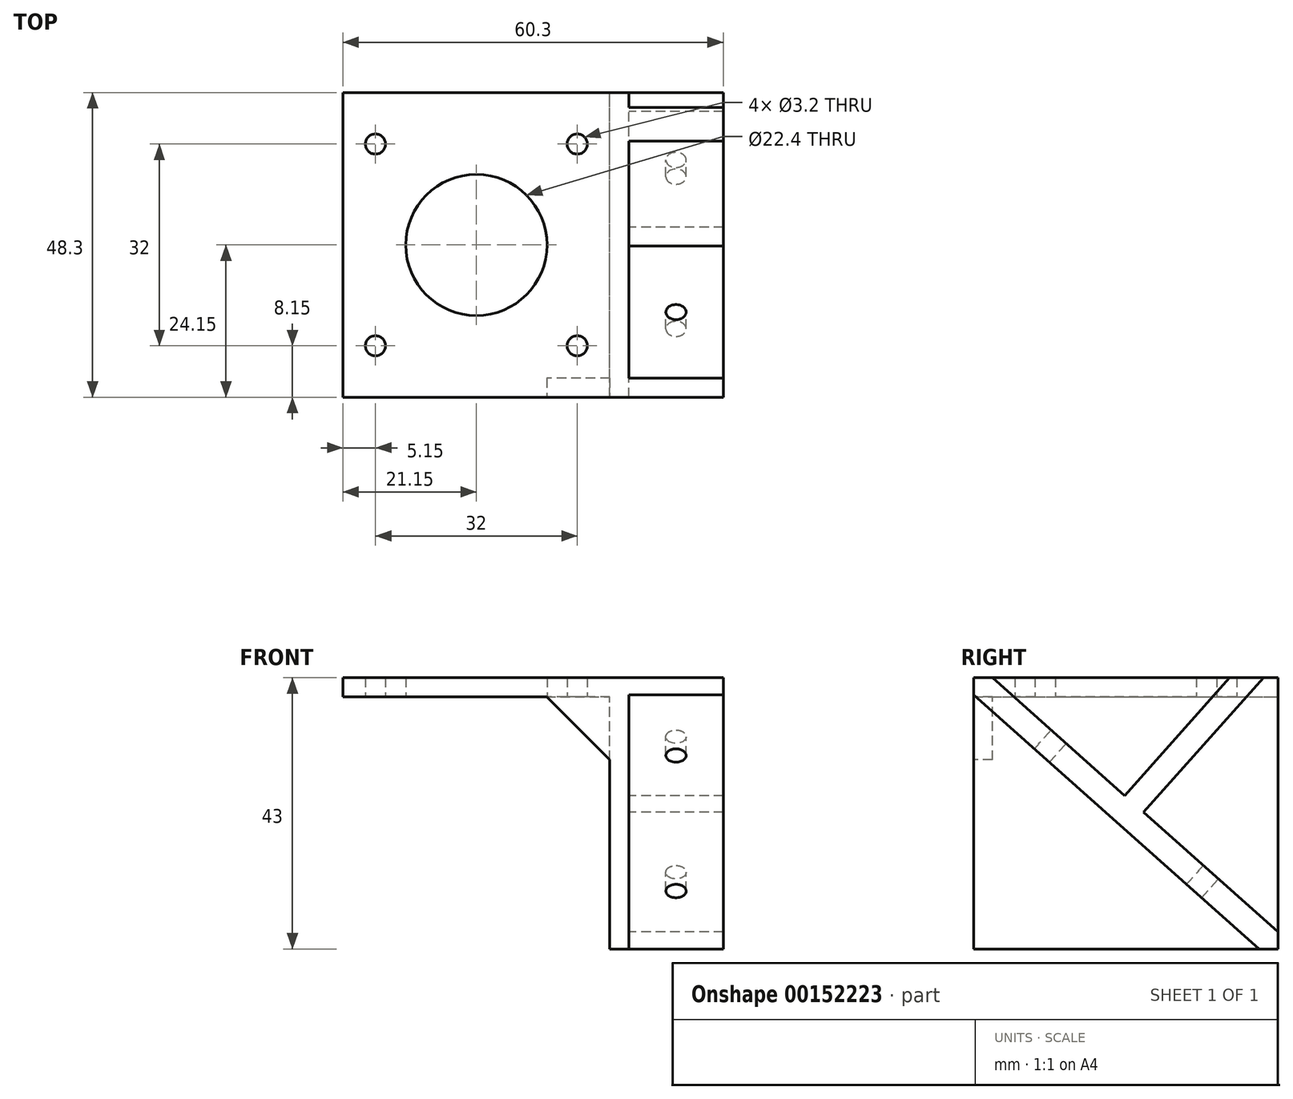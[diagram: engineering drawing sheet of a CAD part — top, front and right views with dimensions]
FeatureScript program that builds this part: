
annotation { "Feature Type Name" : "Feature", "Feature Type Description" : "" }
export const myFeature = defineFeature(function(context is Context, id is Id, definition is map)
    precondition{}
    {
        {
            var Q0;
            Q0=qCreatedBy(makeId("Top.planeOp"),FACE);
            var sketch = newSketch(context, id + "F0", { "sketchPlane" : qUnion([Q0])});
            skCircle(sketch, "E0", {"center": v(0, 0) * mm, "radius": 11.2 * mm});
            skLineSegment(sketch, "E1.bottom", {"start": v(21.15, 21.15) * mm, "end": v(-21.15, 21.15) * mm});
            skLineSegment(sketch, "E1.top", {"start": v(21.15, -21.15) * mm, "end": v(-21.15, -21.15) * mm});
            skLineSegment(sketch, "E1.left", {"start": v(21.15, 21.15) * mm, "end": v(21.15, -21.15) * mm});
            skLineSegment(sketch, "E1.right", {"start": v(-21.15, 21.15) * mm, "end": v(-21.15, -21.15) * mm});
            skLineSegment(sketch, "E2.bottom", {"start": v(16, 16) * mm, "end": v(-16, 16) * mm});
            skLineSegment(sketch, "E2.top", {"start": v(16, -16) * mm, "end": v(-16, -16) * mm});
            skLineSegment(sketch, "E2.left", {"start": v(16, 16) * mm, "end": v(16, -16) * mm});
            skLineSegment(sketch, "E2.right", {"start": v(-16, 16) * mm, "end": v(-16, -16) * mm});
            skCircle(sketch, "E3", {"center": v(-16, 16) * mm, "radius": 1.6 * mm});
            skCircle(sketch, "E4", {"center": v(-16, -16) * mm, "radius": 1.6 * mm});
            skCircle(sketch, "E5", {"center": v(16, -16) * mm, "radius": 1.6 * mm});
            skCircle(sketch, "E6", {"center": v(16, 16) * mm, "radius": 1.6 * mm});
            skLineSegment(sketch, "E7.bottom", {"start": v(-21.15, 21.15) * mm, "end": v(21.15, 21.15) * mm});
            skLineSegment(sketch, "E7.top", {"start": v(-21.15, 24.15) * mm, "end": v(21.15, 24.15) * mm});
            skLineSegment(sketch, "E7.left", {"start": v(-21.15, 21.15) * mm, "end": v(-21.15, 24.15) * mm});
            skLineSegment(sketch, "E7.right", {"start": v(21.15, 21.15) * mm, "end": v(21.15, 24.15) * mm});
            skLineSegment(sketch, "E8.bottom", {"start": v(-21.15, -21.15) * mm, "end": v(21.15, -21.15) * mm});
            skLineSegment(sketch, "E8.top", {"start": v(-21.15, -24.15) * mm, "end": v(21.15, -24.15) * mm});
            skLineSegment(sketch, "E8.left", {"start": v(-21.15, -21.15) * mm, "end": v(-21.15, -24.15) * mm});
            skLineSegment(sketch, "E8.right", {"start": v(21.15, -21.15) * mm, "end": v(21.15, -24.15) * mm});
            skLineSegment(sketch, "E9.bottom", {"start": v(21.15, 24.15) * mm, "end": v(24.15, 24.15) * mm});
            skLineSegment(sketch, "E9.top", {"start": v(21.15, -24.15) * mm, "end": v(24.15, -24.15) * mm});
            skLineSegment(sketch, "E9.left", {"start": v(21.15, 24.15) * mm, "end": v(21.15, -24.15) * mm});
            skLineSegment(sketch, "E9.right", {"start": v(24.15, 24.15) * mm, "end": v(24.15, -24.15) * mm});
            skLineSegment(sketch, "E10", {"start": v(21.15, 21.15) * mm, "end": v(11.15, 21.15) * mm});
            skLineSegment(sketch, "E11", {"start": v(21.15, -24.15) * mm, "end": v(9.24, -24.15) * mm});
            skLineSegment(sketch, "E12", {"start": v(11.15, 21.15) * mm, "end": v(11.15, 24.15) * mm});
            skLineSegment(sketch, "E13", {"start": v(11.15, 21.15) * mm, "end": v(11.15, -21.15) * mm, "construction": true});
            skLineSegment(sketch, "E14", {"start": v(11.15, -21.15) * mm, "end": v(11.15, -24.15) * mm});
            skSolve(sketch);
        }
        {
            var Q0;
            Q0 = qSketchRegion(id + "F0", true);
            var Q1;
            Q1=makeQuery(id+"F0.imprint","IMPRINT",FACE,{"disambiguationData":[TD([[makeQuery(id+"F0.imprint","IMPRINT",EDGE,{"derivedFrom":sQuery(id+"F0.wireOp",EDGE,"E0")}),-1.0]])]});
            extrude(context, id + "F1", {"entities" : qUnion([Q0, Q1]), "depth" : 3 * mm});
        }
        {
            var Q0;
            {var subQ3=sQuery(id+"F0.wireOp",EDGE,"E9.bottom");Q0=makeQuery(id+"F0.imprint","IMPRINT",FACE,{"disambiguationData":[TD([[makeQuery(id+"F0.imprint","IMPRINT",EDGE,{"derivedFrom":subQ3}),-1.0]])]});}
            extrude(context, id + "F2", {"entities" : qUnion([Q0]), "operationType" : NewBodyOperationType.ADD, "oppositeDirection" : true, "depth" : 40 * mm});
        }
        {
            var Q0;
            {var subQ0=sQuery(id+"F0.wireOp",EDGE,"E9.right");Q0=makeQuery(id+"F2.boolean.opBoolean","MERGE",FACE,{"derivedFrom":[makeQuery(id+"F1.opExtrude","SWEPT_FACE",FACE,{"disambiguationData":[OSD([subQ0])]}),makeQuery(id+"F2.opExtrude","SWEPT_FACE",FACE,{"disambiguationData":[OSD([subQ0])]})]});}
            var sketch = newSketch(context, id + "F3", { "sketchPlane" : qUnion([Q0])});
            skLineSegment(sketch, "E15", {"start": v(-24.15, 3) * mm, "end": v(24.15, -40) * mm});
            skLineSegment(sketch, "E16", {"start": v(0, -18.5) * mm, "end": v(1.33, -17) * mm});
            skLineSegment(sketch, "E17", {"start": v(0, -18.5) * mm, "end": v(-1.33, -20) * mm});
            skLineSegment(sketch, "E18", {"start": v(1.33, -17) * mm, "end": v(24.15, -37.32) * mm});
            skLineSegment(sketch, "E19", {"start": v(24.15, -37.32) * mm, "end": v(-21.14, 3) * mm});
            skLineSegment(sketch, "E20", {"start": v(-1.33, -20) * mm, "end": v(21.14, -40) * mm});
            skLineSegment(sketch, "E21", {"start": v(21.14, -40) * mm, "end": v(-24.15, 0.32) * mm});
            skLineSegment(sketch, "E22", {"start": v(1.33, -17) * mm, "end": v(19.14, 3) * mm});
            skPoint(sketch, "E22.endSnap0", {"position": v(0, 3) * mm});
            skLineSegment(sketch, "E23", {"start": v(1.33, -17) * mm, "end": v(2.82, -18.34) * mm});
            skLineSegment(sketch, "E24", {"start": v(1.33, -17) * mm, "end": v(-0.16, -15.68) * mm});
            skLineSegment(sketch, "E25", {"start": v(2.82, -18.34) * mm, "end": v(21.82, 3) * mm});
            skLineSegment(sketch, "E26", {"start": v(-0.16, -15.68) * mm, "end": v(16.46, 3) * mm});
            skSolve(sketch);
        }
        {
            var Q0;
            {var subQ0=sQuery(id+"F3.wireOp",EDGE,"E22");Q0=makeQuery(id+"F3.imprint","IMPRINT",FACE,{"disambiguationData":[TD([[makeQuery(id+"F3.imprint","IMPRINT",EDGE,{"derivedFrom":subQ0}),1.0]])]});}
            var Q1;
            {var subQ0=sQuery(id+"F3.wireOp",EDGE,"E22");Q1=makeQuery(id+"F3.imprint","IMPRINT",FACE,{"disambiguationData":[TD([[makeQuery(id+"F3.imprint","IMPRINT",EDGE,{"derivedFrom":subQ0}),-1.0]])]});}
            var Q2;
            {var subQ6=sQuery(id+"F3.wireOp",EDGE,"E16");Q2=makeQuery(id+"F3.imprint","IMPRINT",FACE,{"disambiguationData":[TD([[makeQuery(id+"F3.imprint","IMPRINT",EDGE,{"derivedFrom":subQ6}),-1.0]])]});}
            var Q3;
            {var subQ5=sQuery(id+"F3.wireOp",EDGE,"E17");Q3=makeQuery(id+"F3.imprint","IMPRINT",FACE,{"disambiguationData":[TD([[makeQuery(id+"F3.imprint","IMPRINT",EDGE,{"derivedFrom":subQ5}),1.0]])]});}
            var Q4;
            {var subQ5=sQuery(id+"F3.wireOp",EDGE,"E17");Q4=makeQuery(id+"F3.imprint","IMPRINT",FACE,{"disambiguationData":[TD([[makeQuery(id+"F3.imprint","IMPRINT",EDGE,{"derivedFrom":subQ5}),-1.0]])]});}
            var Q5;
            {var subQ8=sQuery(id+"F3.wireOp",EDGE,"E16");Q5=makeQuery(id+"F3.imprint","IMPRINT",FACE,{"disambiguationData":[TD([[makeQuery(id+"F3.imprint","IMPRINT",EDGE,{"derivedFrom":subQ8}),1.0]])]});}
            extrude(context, id + "F4", {"entities" : qUnion([Q0, Q1, Q2, Q3, Q4, Q5]), "operationType" : NewBodyOperationType.ADD, "depth" : 15 * mm});
        }
        {
            var Q0;
            {var subQ4=sQuery(id+"F0.wireOp",EDGE,"E10");Q0=makeQuery(id+"F0.imprint","IMPRINT",FACE,{"disambiguationData":[TD([[makeQuery(id+"F0.imprint","IMPRINT",EDGE,{"derivedFrom":subQ4}),-1.0]])]});}
            var Q1;
            {var subQ3=sQuery(id+"F0.wireOp",EDGE,"E14");Q1=makeQuery(id+"F0.imprint","IMPRINT",FACE,{"disambiguationData":[TD([[makeQuery(id+"F0.imprint","IMPRINT",EDGE,{"derivedFrom":subQ3}),1.0]])]});}
            extrude(context, id + "F5", {"entities" : qUnion([Q0, Q1]), "operationType" : NewBodyOperationType.ADD, "oppositeDirection" : true, "depth" : 10 * mm});
        }
        {
            var Q0;
            Q0=makeQuery(id+"F5.opExtrude","CAP_EDGE",EDGE,{"disambiguationData":[OSD([sQuery(id+"F0.wireOp",EDGE,"E12")])],"isStart":false});
            var Q1;
            Q1=makeQuery(id+"F5.opExtrude","CAP_EDGE",EDGE,{"disambiguationData":[OSD([sQuery(id+"F0.wireOp",EDGE,"E14")])],"isStart":false});
            chamfer(context, id + "F6", {"entities" : qUnion([Q0, Q1]), "width" : 10 * mm, "tangentPropagation" : true});
        }
        {
            var Q0;
            {var subQ0=sQuery(id+"F3.wireOp",EDGE,"E19");Q0=makeQuery(id+"F4.opExtrude","SWEPT_FACE",FACE,{"disambiguationData":[OSD([subQ0]),TDD([makeQuery(id+"F3.imprint","IMPRINT",EDGE,{"disambiguationData":[TD([[makeQuery(id+"F3.imprint","INTERSECT",VERTEX,{"derivedFrom":[subQ0,sQuery(id+"F3.wireOp",EDGE,"E23"),sQuery(id+"F3.wireOp",EDGE,"E25")]}),1.0]])],"derivedFrom":subQ0})])]});}
            var sketch = newSketch(context, id + "F7", { "sketchPlane" : qUnion([Q0])});
            skLineSegment(sketch, "E27", {"start": v(39.15, 28.58) * mm, "end": v(31.65, 28.58) * mm});
            skPoint(sketch, "E27.endSnap0", {"position": v(31.65, 42.85) * mm});
            skCircle(sketch, "E28", {"center": v(31.65, 28.58) * mm, "radius": 1.6 * mm});
            skSolve(sketch);
        }
        {
            var Q0;
            {var subQ0=sQuery(id+"F3.wireOp",EDGE,"E19");Q0=makeQuery(id+"F4.opExtrude","SWEPT_FACE",FACE,{"disambiguationData":[OSD([subQ0]),TDD([makeQuery(id+"F3.imprint","IMPRINT",EDGE,{"disambiguationData":[TD([[makeQuery(id+"F3.imprint","INTERSECT",VERTEX,{"derivedFrom":[makeQuery(id+"F1.opExtrude","CAP_EDGE",EDGE,{"disambiguationData":[OSD([sQuery(id+"F0.wireOp",EDGE,"E9.right")])],"isStart":false}),subQ0]}),1.0]])],"derivedFrom":subQ0})])]});}
            var sketch = newSketch(context, id + "F8", { "sketchPlane" : qUnion([Q0])});
            skLineSegment(sketch, "E29", {"start": v(39.15, -3.74) * mm, "end": v(31.65, -3.74) * mm});
            skPoint(sketch, "E29.endSnap0", {"position": v(31.65, -17.79) * mm});
            skCircle(sketch, "E30", {"center": v(31.65, -3.74) * mm, "radius": 1.6 * mm});
            skSolve(sketch);
        }
        {
            var Q0;
            Q0=makeQuery(id+"F7.imprint","IMPRINT",FACE,{"disambiguationData":[TD([[makeQuery(id+"F7.imprint","IMPRINT",EDGE,{"derivedFrom":sQuery(id+"F7.wireOp",EDGE,"E28")}),1.0]])]});
            var Q1;
            Q1=makeQuery(id+"F8.imprint","IMPRINT",FACE,{"disambiguationData":[TD([[makeQuery(id+"F8.imprint","IMPRINT",EDGE,{"derivedFrom":sQuery(id+"F8.wireOp",EDGE,"E30")}),1.0]])]});
            extrude(context, id + "F9", {"entities" : qUnion([Q0, Q1]), "operationType" : NewBodyOperationType.REMOVE, "oppositeDirection" : true, "depth" : 25 * mm});
        }
    });
